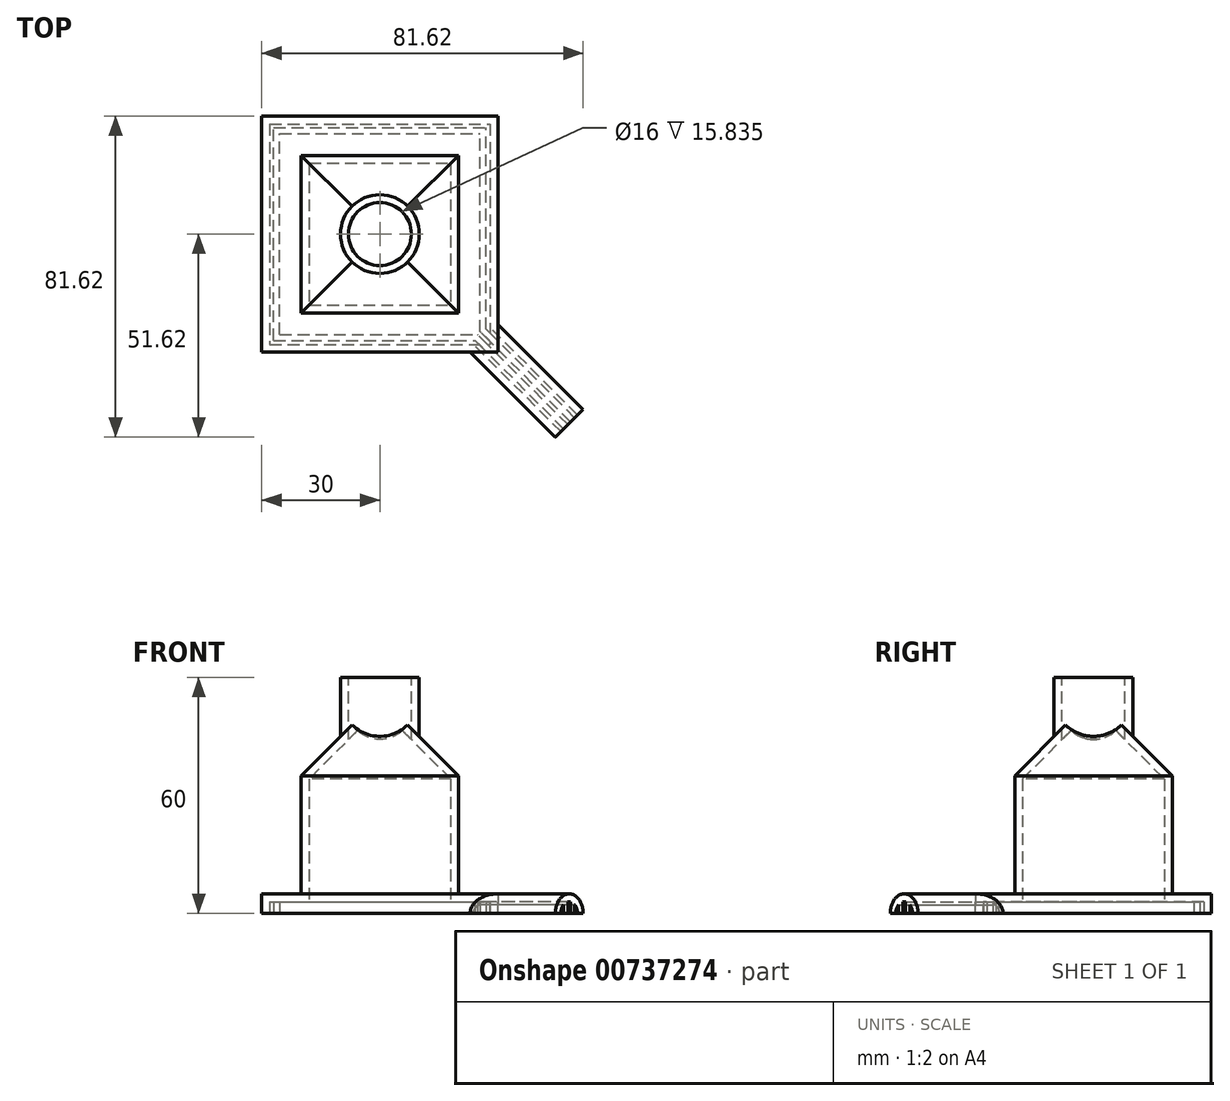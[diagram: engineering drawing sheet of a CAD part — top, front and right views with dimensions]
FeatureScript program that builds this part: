
annotation { "Feature Type Name" : "Feature", "Feature Type Description" : "" }
export const myFeature = defineFeature(function(context is Context, id is Id, definition is map)
    precondition{}
    {
        {
            var Q0;
            Q0=qCreatedBy(makeId("Top.planeOp"),FACE);
            var sketch = newSketch(context, id + "F0", { "sketchPlane" : qUnion([Q0])});
            skLineSegment(sketch, "E0.bottom", {"start": v(-30, 30) * mm, "end": v(30, 30) * mm});
            skLineSegment(sketch, "E0.top", {"start": v(-30, -30) * mm, "end": v(30, -30) * mm});
            skLineSegment(sketch, "E0.left", {"start": v(-30, 30) * mm, "end": v(-30, -30) * mm});
            skLineSegment(sketch, "E0.right", {"start": v(30, 30) * mm, "end": v(30, -30) * mm});
            skSolve(sketch);
        }
        {
            var Q0;
            Q0 = qSketchRegion(id + "F0", true);
            extrude(context, id + "F1", {"entities" : qUnion([Q0]), "depth" : 5 * mm, "offsetDistance" : 25 * mm});
        }
        {
            var Q0;
            Q0=makeQuery(id+"F1.opExtrude","CAP_FACE",FACE,{"disambiguationData":[OSD([sQuery(id+"F0.wireOp",EDGE,"E0.bottom"),sQuery(id+"F0.wireOp",EDGE,"E0.top"),sQuery(id+"F0.wireOp",EDGE,"E0.left"),sQuery(id+"F0.wireOp",EDGE,"E0.right")])],"isStart":false});
            var sketch = newSketch(context, id + "F2", { "sketchPlane" : qUnion([Q0])});
            skLineSegment(sketch, "E1.bottom", {"start": v(-20, 20) * mm, "end": v(20, 20) * mm});
            skLineSegment(sketch, "E1.top", {"start": v(-20, -20) * mm, "end": v(20, -20) * mm});
            skLineSegment(sketch, "E1.left", {"start": v(-20, 20) * mm, "end": v(-20, -20) * mm});
            skLineSegment(sketch, "E1.right", {"start": v(20, 20) * mm, "end": v(20, -20) * mm});
            skSolve(sketch);
        }
        {
            var Q0;
            Q0 = qSketchRegion(id + "F2", true);
            extrude(context, id + "F3", {"entities" : qUnion([Q0]), "operationType" : NewBodyOperationType.ADD, "depth" : 50 * mm, "offsetDistance" : 25 * mm});
        }
        {
            var Q0;
            Q0=makeQuery(id+"F3.opExtrude","SWEPT_FACE",FACE,{"disambiguationData":[OSD([sQuery(id+"F2.wireOp",EDGE,"E1.left")])]});
            var sketch = newSketch(context, id + "F4", { "sketchPlane" : qUnion([Q0])});
            skLineSegment(sketch, "E2", {"start": v(0, 55) * mm, "end": v(20, 35) * mm});
            skLineSegment(sketch, "E3", {"start": v(0, 55) * mm, "end": v(20, 55) * mm});
            skLineSegment(sketch, "E4", {"start": v(20, 55) * mm, "end": v(20, 35) * mm});
            skLineSegment(sketch, "E5.MirrorCS", {"start": v(0, 55) * mm, "end": v(-20, 55) * mm});
            skLineSegment(sketch, "E6.MirrorCS", {"start": v(0, 55) * mm, "end": v(-20, 35) * mm});
            skLineSegment(sketch, "E7.MirrorCS", {"start": v(-20, 55) * mm, "end": v(-20, 35) * mm});
            skSolve(sketch);
        }
        {
            var Q0;
            Q0 = qSketchRegion(id + "F4", true);
            extrude(context, id + "F5", {"entities" : qUnion([Q0]), "operationType" : NewBodyOperationType.REMOVE, "oppositeDirection" : true, "depth" : 40 * mm, "offsetDistance" : 25 * mm});
        }
        {
            var Q0;
            Q0=qCreatedBy(makeId("Front.planeOp"),FACE);
            var sketch = newSketch(context, id + "F6", { "sketchPlane" : qUnion([Q0])});
            skLineSegment(sketch, "E8.0", {"start": v(-20, 55) * mm, "end": v(-20, 35) * mm});
            skLineSegment(sketch, "E9.0", {"start": v(20, 55) * mm, "end": v(-20, 55) * mm});
            skLineSegment(sketch, "E10.0", {"start": v(20, 55) * mm, "end": v(20, 35) * mm});
            skLineSegment(sketch, "E11", {"start": v(-20, 35) * mm, "end": v(0, 55) * mm});
            skLineSegment(sketch, "E12", {"start": v(0, 55) * mm, "end": v(-20, 55) * mm});
            skLineSegment(sketch, "E13", {"start": v(0, 55) * mm, "end": v(20, 35) * mm});
            skLineSegment(sketch, "E14", {"start": v(20, 55) * mm, "end": v(0, 55) * mm});
            skSolve(sketch);
        }
        {
            var Q0;
            {var subQ4=sQuery(id+"F6.wireOp",EDGE,"E10.0");var subQ5=sQuery(id+"F6.wireOp",EDGE,"E8.0");Q0=qUnion([makeQuery(id+"F6.imprint","IMPRINT",FACE,{"disambiguationData":[TD([[makeQuery(id+"F6.imprint","IMPRINT",EDGE,{"derivedFrom":subQ5}),1.0]])]}),makeQuery(id+"F6.imprint","IMPRINT",FACE,{"disambiguationData":[TD([[makeQuery(id+"F6.imprint","IMPRINT",EDGE,{"derivedFrom":subQ4}),-1.0]])]})]);}
            extrude(context, id + "F7", {"entities" : qUnion([Q0]), "operationType" : NewBodyOperationType.REMOVE, "oppositeDirection" : true, "depth" : 20 * mm, "offsetDistance" : 25 * mm, "hasSecondDirection" : true, "secondDirectionOppositeDirection" : false, "secondDirectionDepth" : 20 * mm});
        }
        {
            var Q0;
            Q0=qCreatedBy(makeId("Top.planeOp"),FACE);
            cPlane(context, id + "F8", {"entities" : qUnion([Q0]), "cplaneType" : CPlaneType.OFFSET, "offset" : 60 * mm, "width" : 150 * mm, "height" : 150 * mm});
        }
        {
            var Q0;
            Q0=qCreatedBy(id+"F8.planeOp",FACE);
            var sketch = newSketch(context, id + "F9", { "sketchPlane" : qUnion([Q0])});
            skCircle(sketch, "E15", {"center": v(0, 0) * mm, "radius": 10 * mm});
            skSolve(sketch);
        }
        {
            var Q0;
            Q0=makeQuery(id+"F9.imprint","IMPRINT",FACE,{"disambiguationData":[TD([[makeQuery(id+"F9.imprint","IMPRINT",EDGE,{"derivedFrom":sQuery(id+"F9.wireOp",EDGE,"E15")}),1.0]])]});
            var Q1;
            Q1=makeQuery(id+"F1.opExtrude","CAP_FACE",FACE,{"disambiguationData":[OSD([sQuery(id+"F0.wireOp",EDGE,"E0.bottom"),sQuery(id+"F0.wireOp",EDGE,"E0.top"),sQuery(id+"F0.wireOp",EDGE,"E0.left"),sQuery(id+"F0.wireOp",EDGE,"E0.right")])],"isStart":true});
            extrude(context, id + "F10", {"entities" : qUnion([Q0]), "operationType" : NewBodyOperationType.ADD, "endBound" : BoundingType.UP_TO_SURFACE, "oppositeDirection" : true, "depth" : 25 * mm, "endBoundEntityFace" : qUnion([Q1]), "offsetDistance" : 25 * mm});
        }
        {
            var Q0;
            Q0=makeQuery(id+"F1.opExtrude","CAP_FACE",FACE,{"disambiguationData":[OSD([sQuery(id+"F0.wireOp",EDGE,"E0.bottom"),sQuery(id+"F0.wireOp",EDGE,"E0.top"),sQuery(id+"F0.wireOp",EDGE,"E0.left"),sQuery(id+"F0.wireOp",EDGE,"E0.right")])],"isStart":true});
            var Q1;
            Q1=makeQuery(id+"F10.opExtrude","CAP_FACE",FACE,{"disambiguationData":[OSD([sQuery(id+"F9.wireOp",EDGE,"E15")])],"isStart":true});
            var Q2;
            Q2=makeQuery(id+"F1.opExtrude","SWEPT_BODY",BODY,{"disambiguationData":[OSD([sQuery(id+"F0.wireOp",EDGE,"E0.bottom"),sQuery(id+"F0.wireOp",EDGE,"E0.top"),sQuery(id+"F0.wireOp",EDGE,"E0.left"),sQuery(id+"F0.wireOp",EDGE,"E0.right")])]});
            shell(context, id + "F11", {"entities" : qUnion([Q0, Q1]), "parts" : qUnion([Q2]), "thickness" : 2 * mm});
        }
        {
            var Q0;
            Q0=qCreatedBy(makeId("Right.planeOp"),FACE);
            var Q1;
            Q1=qCreatedBy(makeId("Front.planeOp"),FACE);
            cPlane(context, id + "F12", {"entities" : qUnion([Q0, Q1]), "cplaneType" : CPlaneType.MID_PLANE, "offset" : 25 * mm, "flipAlignment" : true, "width" : 150 * mm, "height" : 150 * mm});
        }
        {
            var Q0;
            Q0=qCreatedBy(id+"F12.planeOp",FACE);
            cPlane(context, id + "F13", {"entities" : qUnion([Q0]), "cplaneType" : CPlaneType.OFFSET, "offset" : 43 * mm, "width" : 150 * mm, "height" : 150 * mm});
        }
        {
            var Q0;
            Q0=qCreatedBy(id+"F13.planeOp",FACE);
            var sketch = newSketch(context, id + "F14", { "sketchPlane" : qUnion([Q0])});
            skPoint(sketch, "E16.0", {"position": v(0, 5) * mm});
            skArc(sketch, "E17", {"start": v(5, 0) * mm, "mid": v(0, 5) * mm, "end": v(-5, 0) * mm});
            skArc(sketch, "E18.0", {"start": v(3, 0) * mm, "mid": v(0, 3) * mm, "end": v(-3, 0) * mm});
            skLineSegment(sketch, "E19.0", {"start": v(5, 0) * mm, "end": v(3, 0) * mm});
            skLineSegment(sketch, "E20.0", {"start": v(-5, 0) * mm, "end": v(-3, 0) * mm});
            skPoint(sketch, "E21.orphan", {"position": v(-42.43, 0) * mm});
            skPoint(sketch, "E22.orphan", {"position": v(42.43, 0) * mm});
            skSolve(sketch);
        }
        {
            var Q0;
            Q0=makeQuery(id+"F14.imprint","IMPRINT",FACE,{"disambiguationData":[TD([[makeQuery(id+"F14.imprint","IMPRINT",EDGE,{"derivedFrom":sQuery(id+"F14.wireOp",EDGE,"E17")}),1.0]])]});
            extrude(context, id + "F15", {"entities" : qUnion([Q0]), "operationType" : NewBodyOperationType.ADD, "depth" : 25 * mm, "offsetDistance" : 25 * mm, "hasSecondDirection" : true, "secondDirectionBound" : SecondDirectionBoundingType.UP_TO_NEXT, "secondDirectionOppositeDirection" : true, "secondDirectionDepth" : 25 * mm});
        }
        {
            var Q0;
            Q0=makeQuery(id+"F15.opExtrude","CAP_FACE",FACE,{"disambiguationData":[OSD([sQuery(id+"F14.wireOp",EDGE,"E17"),sQuery(id+"F14.wireOp",EDGE,"E18.0"),sQuery(id+"F14.wireOp",EDGE,"E19.0"),sQuery(id+"F14.wireOp",EDGE,"E20.0")])],"isStart":false});
            var sketch = newSketch(context, id + "F16", { "sketchPlane" : qUnion([Q0])});
            skArc(sketch, "E23.0", {"start": v(3, 0) * mm, "mid": v(0, 3) * mm, "end": v(-3, 0) * mm});
            skLineSegment(sketch, "E24.0", {"start": v(-3, 0) * mm, "end": v(0, 0) * mm});
            skLineSegment(sketch, "E25.0", {"start": v(3, 0) * mm, "end": v(0, 0) * mm});
            skSolve(sketch);
        }
        {
            var Q0;
            Q0=makeQuery(id+"F16.imprint","IMPRINT",FACE,{"disambiguationData":[TD([[makeQuery(id+"F16.imprint","IMPRINT",EDGE,{"derivedFrom":sQuery(id+"F16.wireOp",EDGE,"E23.0")}),1.0]])]});
            extrude(context, id + "F17", {"entities" : qUnion([Q0]), "operationType" : NewBodyOperationType.REMOVE, "oppositeDirection" : true, "depth" : 55.3 * mm, "offsetDistance" : 25 * mm});
        }
        {
            var Q0;
            Q0=makeQuery(id+"F15.boolean.opBoolean","MERGE",FACE,{"derivedFrom":[makeQuery(id+"F1.opExtrude","CAP_FACE",FACE,{"disambiguationData":[OSD([sQuery(id+"F0.wireOp",EDGE,"E0.bottom"),sQuery(id+"F0.wireOp",EDGE,"E0.top"),sQuery(id+"F0.wireOp",EDGE,"E0.left"),sQuery(id+"F0.wireOp",EDGE,"E0.right")])],"isStart":true}),makeQuery(id+"F15.opExtrude","SWEPT_FACE",FACE,{"disambiguationData":[OSD([sQuery(id+"F14.wireOp",EDGE,"E19.0")])]}),makeQuery(id+"F15.opExtrude","SWEPT_FACE",FACE,{"disambiguationData":[OSD([sQuery(id+"F14.wireOp",EDGE,"E20.0")])]})]});
            var sketch = newSketch(context, id + "F18", { "sketchPlane" : qUnion([Q0])});
            skLineSegment(sketch, "E26.bottom", {"start": v(-27, 27) * mm, "end": v(24.17, 27) * mm});
            skLineSegment(sketch, "E26.top", {"start": v(-27, -27) * mm, "end": v(27, -27) * mm});
            skLineSegment(sketch, "E26.left", {"start": v(-27, 27) * mm, "end": v(-27, -27) * mm});
            skLineSegment(sketch, "E26.right", {"start": v(27, 24.17) * mm, "end": v(27, -27) * mm});
            skLineSegment(sketch, "E27.bottom", {"start": v(-25.5, 25.5) * mm, "end": v(24.8, 25.5) * mm});
            skLineSegment(sketch, "E27.top", {"start": v(-25.5, -25.5) * mm, "end": v(25.5, -25.5) * mm});
            skLineSegment(sketch, "E27.left", {"start": v(-25.5, 25.5) * mm, "end": v(-25.5, -25.5) * mm});
            skLineSegment(sketch, "E27.right", {"start": v(25.5, 24.8) * mm, "end": v(25.5, -25.5) * mm});
            skLineSegment(sketch, "E28.0", {"start": v(45.96, 50.2) * mm, "end": v(23.76, 28) * mm});
            skLineSegment(sketch, "E29.0", {"start": v(50.2, 45.96) * mm, "end": v(28, 23.76) * mm});
            skLineSegment(sketch, "E30.0", {"start": v(49.5, 46.67) * mm, "end": v(27, 24.17) * mm});
            skLineSegment(sketch, "E31.0", {"start": v(46.67, 49.5) * mm, "end": v(24.17, 27) * mm});
            skLineSegment(sketch, "E32.0", {"start": v(48.44, 47.73) * mm, "end": v(25.5, 24.8) * mm});
            skLineSegment(sketch, "E33.0", {"start": v(47.73, 48.44) * mm, "end": v(24.8, 25.5) * mm});
            skLineSegment(sketch, "E34", {"start": v(46.67, 49.5) * mm, "end": v(47.73, 48.44) * mm});
            skLineSegment(sketch, "E35", {"start": v(48.44, 47.73) * mm, "end": v(49.5, 46.67) * mm});
            skSolve(sketch);
        }
        {
            var Q0;
            Q0 = qSketchRegion(id + "F18", true);
            extrude(context, id + "F19", {"entities" : qUnion([Q0]), "operationType" : NewBodyOperationType.ADD, "endBound" : BoundingType.UP_TO_NEXT, "oppositeDirection" : true, "depth" : 25 * mm, "offsetDistance" : 25 * mm});
        }
    });
